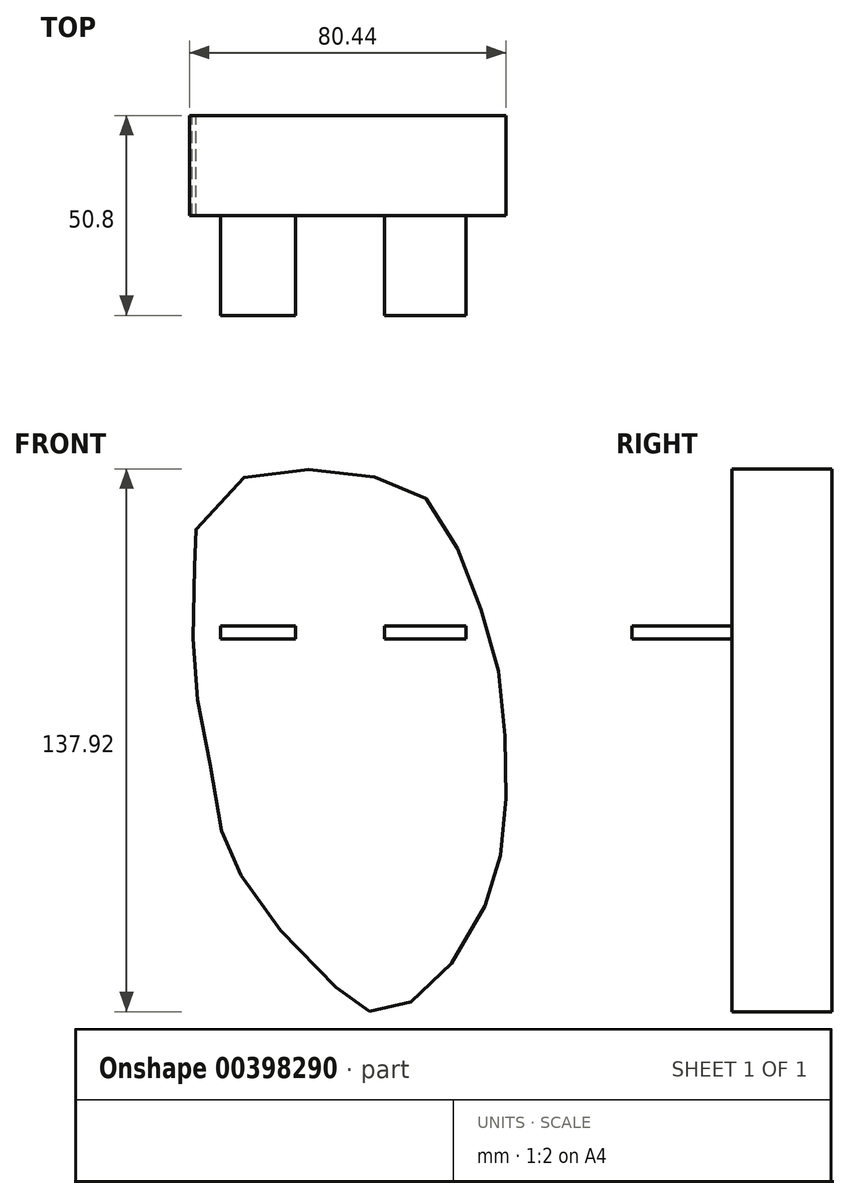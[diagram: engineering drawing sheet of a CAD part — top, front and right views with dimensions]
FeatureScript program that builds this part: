
annotation { "Feature Type Name" : "Feature", "Feature Type Description" : "" }
export const myFeature = defineFeature(function(context is Context, id is Id, definition is map)
    precondition{}
    {
        {
            var Q0;
            Q0=qCreatedBy(makeId("Front.planeOp"),FACE);
            var sketch = newSketch(context, id + "F0", { "sketchPlane" : qUnion([Q0])});
            skFitSpline(sketch, "E0", {"points": [v(-43.83, 49) * mm, v(-44.48, 24.05) * mm, v(-41.87, 10.14) * mm, v(-37.81, -14.55) * mm, v(-34.16, -25.39) * mm, v(-24.43, -40.53) * mm, v(-5.32, -60.26) * mm, v(0, -63.77) * mm, v(7.84, -62.87) * mm, v(17.58, -56.44) * mm, v(29.1, -38.79) * mm, v(33.55, -25.75) * mm, v(35.16, -10.54) * mm, v(34.84, 8.07) * mm, v(32.13, 28.18) * mm, v(25.61, 46.68) * mm, v(17.44, 63.86) * mm, v(5.5, 71.03) * mm, v(-14.62, 73.8) * mm, v(-34.23, 70.05) * mm, v(-45.17, 53.58) * mm, v(-43.83, 49) * mm]});
            skSolve(sketch);
        }
        {
            var Q0;
            Q0=makeQuery(id+"F0.imprint","IMPRINT",FACE,{"disambiguationData":[TD([[makeQuery(id+"F0.imprint","IMPRINT",EDGE,{"derivedFrom":sQuery(id+"F0.wireOp",EDGE,"E0")}),1.0]])]});
            extrude(context, id + "F1", {"entities" : qUnion([Q0]), "depth" : 25.4 * mm});
        }
        {
            var Q0;
            Q0=makeQuery(id+"F1.opExtrude","CAP_FACE",FACE,{"disambiguationData":[OSD([sQuery(id+"F0.wireOp",EDGE,"E0")])],"isStart":false});
            var sketch = newSketch(context, id + "F2", { "sketchPlane" : qUnion([Q0])});
            skLineSegment(sketch, "E1.bottom", {"start": v(-18.22, 30.77) * mm, "end": v(-37.32, 30.77) * mm});
            skLineSegment(sketch, "E1.top", {"start": v(-18.22, 34.04) * mm, "end": v(-37.32, 34.04) * mm});
            skLineSegment(sketch, "E1.left", {"start": v(-18.22, 30.77) * mm, "end": v(-18.22, 34.04) * mm});
            skLineSegment(sketch, "E1.right", {"start": v(-37.32, 30.77) * mm, "end": v(-37.32, 34.04) * mm});
            skSolve(sketch);
        }
        {
            var Q0;
            Q0=makeQuery(id+"F2.imprint","IMPRINT",FACE,{"disambiguationData":[TD([[makeQuery(id+"F2.imprint","IMPRINT",EDGE,{"derivedFrom":sQuery(id+"F2.wireOp",EDGE,"E1.bottom")}),-1.0]])]});
            extrude(context, id + "F3", {"entities" : qUnion([Q0]), "operationType" : NewBodyOperationType.ADD, "depth" : 25.4 * mm});
        }
        {
            var Q0;
            Q0=makeQuery(id+"F1.opExtrude","CAP_FACE",FACE,{"disambiguationData":[OSD([sQuery(id+"F0.wireOp",EDGE,"E0")])],"isStart":false});
            var sketch = newSketch(context, id + "F4", { "sketchPlane" : qUnion([Q0])});
            skLineSegment(sketch, "E2.bottom", {"start": v(4.34, 30.77) * mm, "end": v(25.07, 30.77) * mm});
            skLineSegment(sketch, "E2.top", {"start": v(4.34, 34.04) * mm, "end": v(25.07, 34.04) * mm});
            skLineSegment(sketch, "E2.left", {"start": v(4.34, 30.77) * mm, "end": v(4.34, 34.04) * mm});
            skLineSegment(sketch, "E2.right", {"start": v(25.07, 30.77) * mm, "end": v(25.07, 34.04) * mm});
            skSolve(sketch);
        }
        {
            var Q0;
            Q0=makeQuery(id+"F4.imprint","IMPRINT",FACE,{"disambiguationData":[TD([[makeQuery(id+"F4.imprint","IMPRINT",EDGE,{"derivedFrom":sQuery(id+"F4.wireOp",EDGE,"E2.bottom")}),1.0]])]});
            extrude(context, id + "F5", {"entities" : qUnion([Q0]), "operationType" : NewBodyOperationType.ADD, "depth" : 25.4 * mm});
        }
    });
